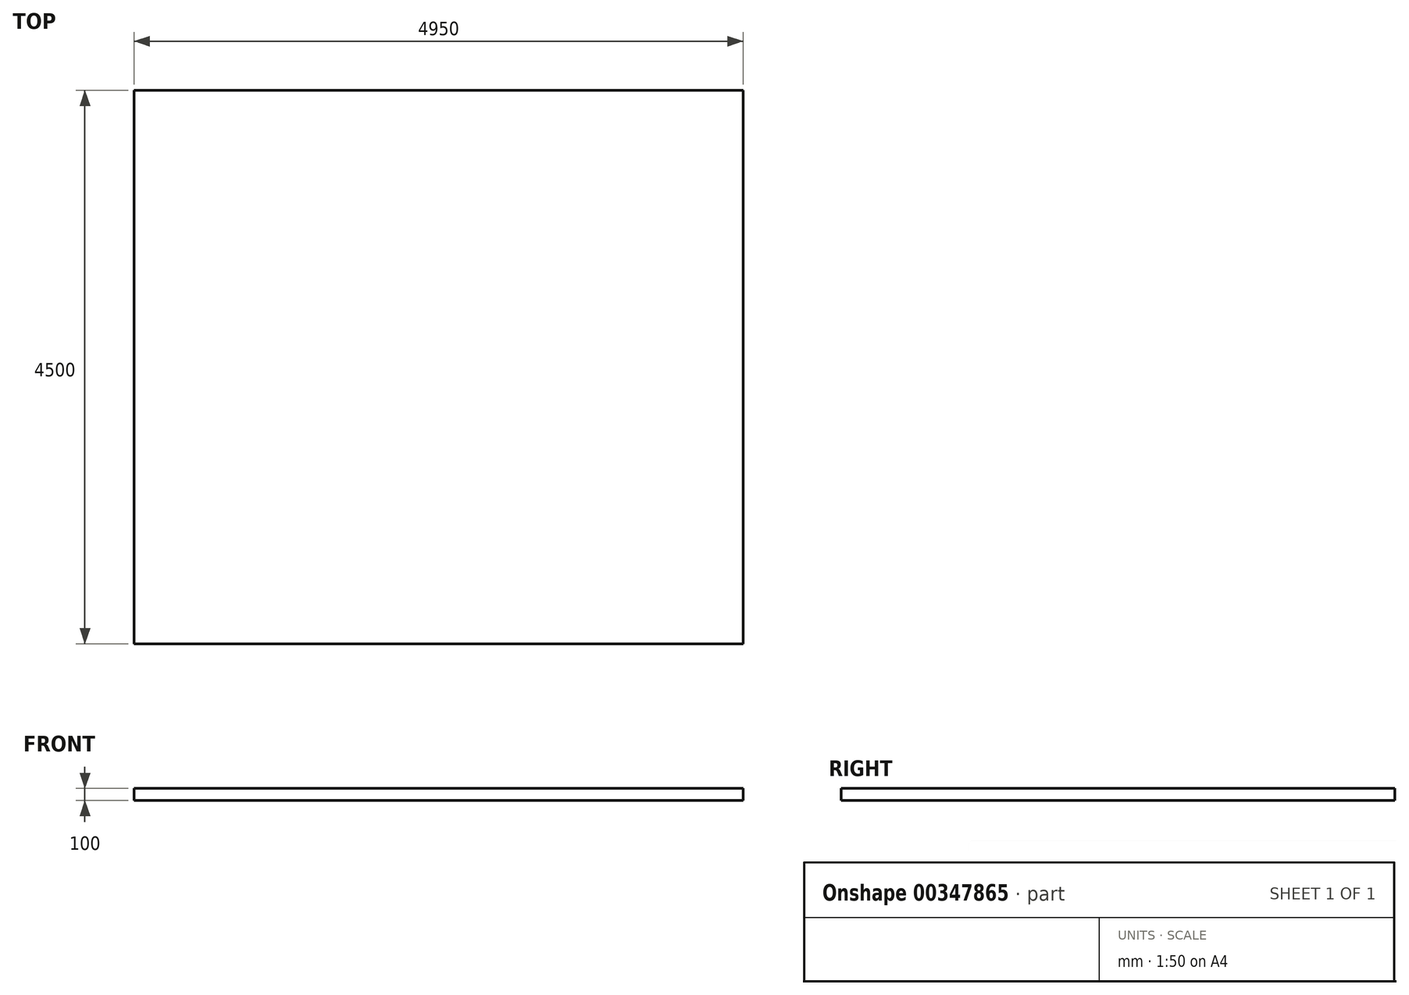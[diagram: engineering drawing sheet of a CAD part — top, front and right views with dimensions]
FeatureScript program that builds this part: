
annotation { "Feature Type Name" : "Feature", "Feature Type Description" : "" }
export const myFeature = defineFeature(function(context is Context, id is Id, definition is map)
    precondition{}
    {
        {
            var Q0;
            Q0=qCreatedBy(makeId("Top.planeOp"),FACE);
            var sketch = newSketch(context, id + "F0", { "sketchPlane" : qUnion([Q0])});
            skLineSegment(sketch, "E0.bottom", {"start": v(0, 0) * mm, "end": v(4950, 0) * mm});
            skLineSegment(sketch, "E0.top", {"start": v(0, 4500) * mm, "end": v(4950, 4500) * mm});
            skLineSegment(sketch, "E0.left", {"start": v(0, 0) * mm, "end": v(0, 4500) * mm});
            skLineSegment(sketch, "E0.right", {"start": v(4950, 0) * mm, "end": v(4950, 4500) * mm});
            skSolve(sketch);
        }
        {
            var Q0;
            Q0=makeQuery(id+"F0.imprint","IMPRINT",FACE,{"disambiguationData":[TD([[makeQuery(id+"F0.imprint","IMPRINT",EDGE,{"derivedFrom":sQuery(id+"F0.wireOp",EDGE,"E0.bottom")}),1.0]])]});
            extrude(context, id + "F1", {"entities" : qUnion([Q0]), "oppositeDirection" : true, "depth" : 100 * mm});
        }
    });
